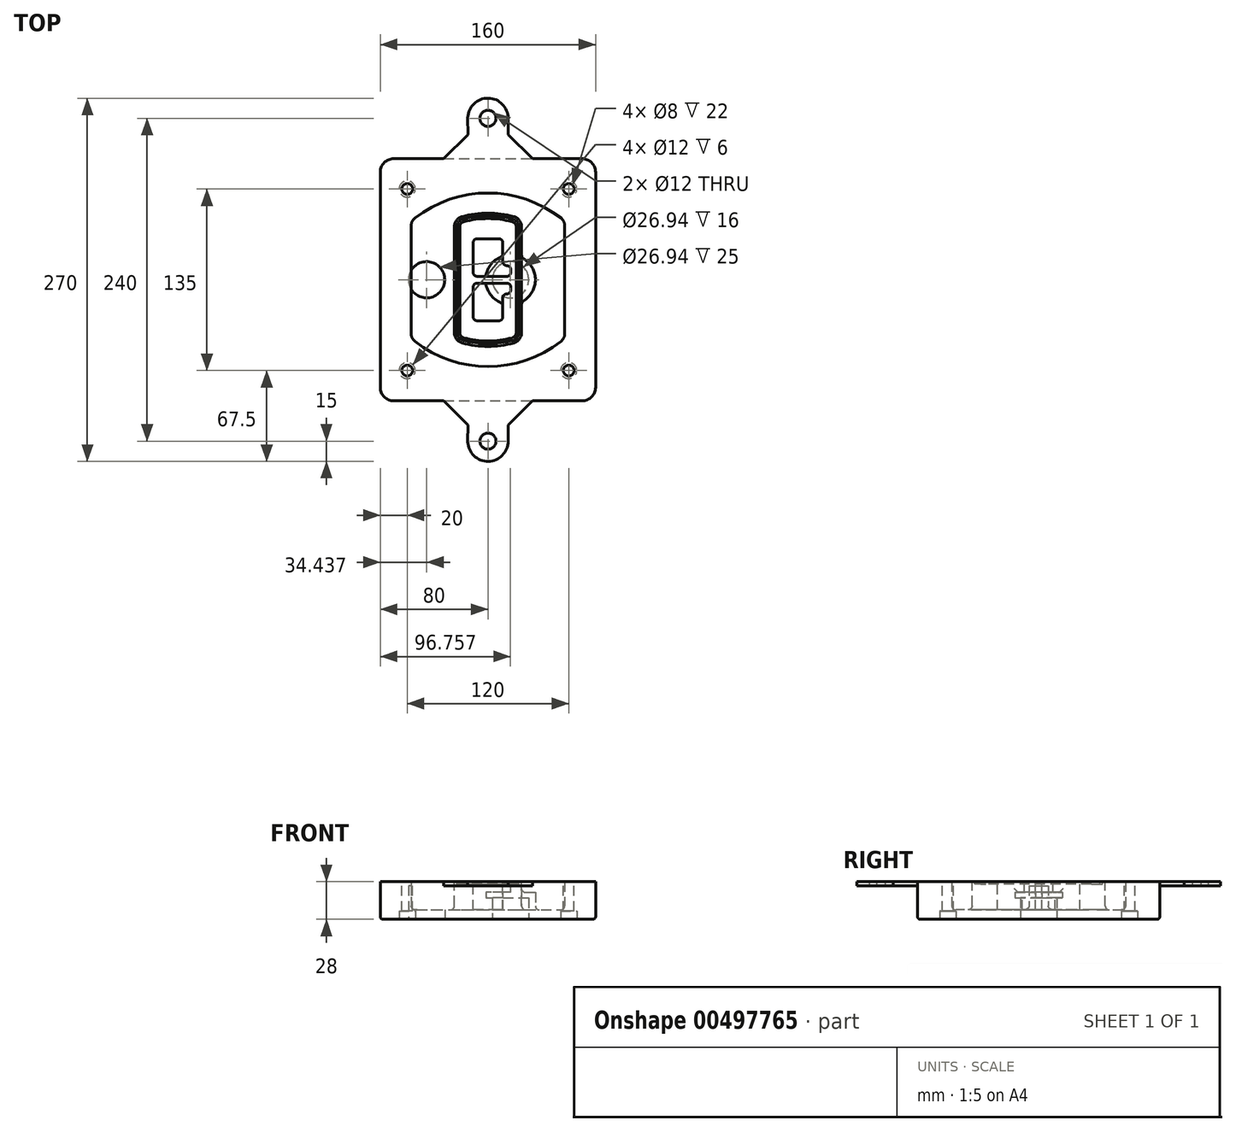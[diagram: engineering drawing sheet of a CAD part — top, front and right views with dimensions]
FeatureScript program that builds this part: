
annotation { "Feature Type Name" : "Feature", "Feature Type Description" : "" }
export const myFeature = defineFeature(function(context is Context, id is Id, definition is map)
    precondition{}
    {
        {
            var Q0;
            Q0=qCreatedBy(makeId("Top.planeOp"),FACE);
            var sketch = newSketch(context, id + "F0", { "sketchPlane" : qUnion([Q0])});
            skPoint(sketch, "E0.rect.middle", {"position": v(0, 0) * mm});
            skLineSegment(sketch, "E1.bottom", {"start": v(-70, -90) * mm, "end": v(70, -90) * mm});
            skLineSegment(sketch, "E1.top", {"start": v(-70, 90) * mm, "end": v(70, 90) * mm});
            skLineSegment(sketch, "E1.left", {"start": v(-80, -80) * mm, "end": v(-80, 80) * mm});
            skLineSegment(sketch, "E1.right", {"start": v(80, -80) * mm, "end": v(80, 80) * mm});
            skLineSegment(sketch, "E2", {"start": v(-80, 90) * mm, "end": v(80, -90) * mm, "construction": true});
            skLineSegment(sketch, "E3", {"start": v(80, 90) * mm, "end": v(-80, -90) * mm, "construction": true});
            skCircle(sketch, "E4", {"center": v(-60, 67.5) * mm, "radius": 4 * mm});
            skCircle(sketch, "E5", {"center": v(60, 67.5) * mm, "radius": 4 * mm});
            skCircle(sketch, "E6", {"center": v(60, -67.5) * mm, "radius": 4 * mm});
            skCircle(sketch, "E7", {"center": v(-60, -67.5) * mm, "radius": 4 * mm});
            skLineSegment(sketch, "E8", {"start": v(-60, 67.5) * mm, "end": v(60, 67.5) * mm, "construction": true});
            skLineSegment(sketch, "E9", {"start": v(60, 67.5) * mm, "end": v(60, -67.5) * mm, "construction": true});
            skLineSegment(sketch, "E10", {"start": v(60, -67.5) * mm, "end": v(-60, -67.5) * mm, "construction": true});
            skLineSegment(sketch, "E11", {"start": v(-60, -67.5) * mm, "end": v(-60, 67.5) * mm, "construction": true});
            skLineSegment(sketch, "E12", {"start": v(-60, 40.3) * mm, "end": v(-60, -40.3) * mm});
            skLineSegment(sketch, "E13", {"start": v(60, 40.3) * mm, "end": v(60, -40.3) * mm});
            skArc(sketch, "E14", {"start": v(56.15, 48.18) * mm, "mid": v(0, 67.5) * mm, "end": v(-56.15, 48.18) * mm});
            skArc(sketch, "E15", {"start": v(-56.15, -48.18) * mm, "mid": v(0, -67.5) * mm, "end": v(56.15, -48.18) * mm});
            skLineSegment(sketch, "E16", {"start": v(-60, 0) * mm, "end": v(60, 0) * mm, "construction": true});
            skPoint(sketch, "E17.visualSharp", {"position": v(-60, -45) * mm});
            skArc(sketch, "E17.filletArc", {"start": v(-60, -40.3) * mm, "mid": v(-58.99, -44.68) * mm, "end": v(-56.15, -48.18) * mm});
            skPoint(sketch, "E18.visualSharp", {"position": v(-60, 45) * mm});
            skArc(sketch, "E18.filletArc", {"start": v(-56.15, 48.18) * mm, "mid": v(-58.99, 44.68) * mm, "end": v(-60, 40.3) * mm});
            skPoint(sketch, "E19.visualSharp", {"position": v(60, 45) * mm});
            skArc(sketch, "E19.filletArc", {"start": v(60, 40.3) * mm, "mid": v(58.99, 44.68) * mm, "end": v(56.15, 48.18) * mm});
            skPoint(sketch, "E20.visualSharp", {"position": v(60, -45) * mm});
            skArc(sketch, "E20.filletArc", {"start": v(56.15, -48.18) * mm, "mid": v(58.99, -44.68) * mm, "end": v(60, -40.3) * mm});
            skPoint(sketch, "E21.visualSharp", {"position": v(-80, 90) * mm});
            skArc(sketch, "E21.filletArc", {"start": v(-70, 90) * mm, "mid": v(-77.07, 87.07) * mm, "end": v(-80, 80) * mm});
            skPoint(sketch, "E22.visualSharp", {"position": v(80, 90) * mm});
            skArc(sketch, "E22.filletArc", {"start": v(80, 80) * mm, "mid": v(77.07, 87.07) * mm, "end": v(70, 90) * mm});
            skPoint(sketch, "E23.visualSharp", {"position": v(80, -90) * mm});
            skArc(sketch, "E23.filletArc", {"start": v(70, -90) * mm, "mid": v(77.07, -87.07) * mm, "end": v(80, -80) * mm});
            skPoint(sketch, "E24.visualSharp", {"position": v(-80, -90) * mm});
            skArc(sketch, "E24.filletArc", {"start": v(-80, -80) * mm, "mid": v(-77.07, -87.07) * mm, "end": v(-70, -90) * mm});
            skArc(sketch, "E25.0", {"start": v(57, 40.3) * mm, "mid": v(56.3, 43.36) * mm, "end": v(54.3, 45.81) * mm});
            skLineSegment(sketch, "E25.1", {"start": v(57, 40.3) * mm, "end": v(57, -40.3) * mm});
            skArc(sketch, "E25.2", {"start": v(54.3, -45.81) * mm, "mid": v(56.3, -43.36) * mm, "end": v(57, -40.3) * mm});
            skArc(sketch, "E25.3", {"start": v(-54.3, -45.81) * mm, "mid": v(0, -64.5) * mm, "end": v(54.3, -45.81) * mm});
            skArc(sketch, "E25.4", {"start": v(-57, -40.3) * mm, "mid": v(-56.3, -43.36) * mm, "end": v(-54.3, -45.81) * mm});
            skArc(sketch, "E25.5", {"start": v(54.3, 45.81) * mm, "mid": v(0, 64.5) * mm, "end": v(-54.3, 45.81) * mm});
            skLineSegment(sketch, "E25.6", {"start": v(-57, 40.3) * mm, "end": v(-57, -40.3) * mm});
            skArc(sketch, "E25.7", {"start": v(-54.3, 45.81) * mm, "mid": v(-56.3, 43.36) * mm, "end": v(-57, 40.3) * mm});
            skArc(sketch, "E26.0", {"start": v(-58.62, 51.33) * mm, "mid": v(-62.58, 46.43) * mm, "end": v(-64, 40.3) * mm});
            skArc(sketch, "E26.1", {"start": v(58.62, 51.33) * mm, "mid": v(0, 71.5) * mm, "end": v(-58.62, 51.33) * mm});
            skArc(sketch, "E26.2", {"start": v(64, 40.3) * mm, "mid": v(62.58, 46.43) * mm, "end": v(58.62, 51.33) * mm});
            skLineSegment(sketch, "E26.3", {"start": v(64, 40.3) * mm, "end": v(64, -40.3) * mm});
            skArc(sketch, "E26.4", {"start": v(58.62, -51.33) * mm, "mid": v(62.58, -46.43) * mm, "end": v(64, -40.3) * mm});
            skLineSegment(sketch, "E26.5", {"start": v(-64, 40.3) * mm, "end": v(-64, -40.3) * mm});
            skArc(sketch, "E26.6", {"start": v(-58.62, -51.33) * mm, "mid": v(0, -71.5) * mm, "end": v(58.62, -51.33) * mm});
            skArc(sketch, "E26.7", {"start": v(-64, -40.3) * mm, "mid": v(-62.58, -46.43) * mm, "end": v(-58.62, -51.33) * mm});
            skSolve(sketch);
        }
        {
            var Q0;
            Q0=makeQuery(id+"F0.imprint","IMPRINT",FACE,{"disambiguationData":[TD([[makeQuery(id+"F0.imprint","IMPRINT",EDGE,{"derivedFrom":sQuery(id+"F0.wireOp",EDGE,"E1.bottom")}),1.0]])]});
            var Q1;
            Q1=makeQuery(id+"F0.imprint","IMPRINT",FACE,{"disambiguationData":[TD([[makeQuery(id+"F0.imprint","IMPRINT",EDGE,{"derivedFrom":sQuery(id+"F0.wireOp",EDGE,"E12")}),1.0]])]});
            var Q2;
            Q2=makeQuery(id+"F0.imprint","IMPRINT",FACE,{"disambiguationData":[TD([[makeQuery(id+"F0.imprint","IMPRINT",EDGE,{"derivedFrom":sQuery(id+"F0.wireOp",EDGE,"E25.0")}),1.0]])]});
            var Q3;
            Q3=makeQuery(id+"F0.imprint","IMPRINT",FACE,{"disambiguationData":[TD([[makeQuery(id+"F0.imprint","IMPRINT",EDGE,{"derivedFrom":sQuery(id+"F0.wireOp",EDGE,"E12")}),-1.0]])]});
            extrude(context, id + "F1", {"entities" : qUnion([Q0, Q1, Q2, Q3]), "oppositeDirection" : true, "depth" : 25 * mm});
        }
        {
            var Q0;
            Q0=makeQuery(id+"F0.imprint","IMPRINT",FACE,{"disambiguationData":[TD([[makeQuery(id+"F0.imprint","IMPRINT",EDGE,{"derivedFrom":sQuery(id+"F0.wireOp",EDGE,"E12")}),1.0]])]});
            extrude(context, id + "F2", {"entities" : qUnion([Q0]), "operationType" : NewBodyOperationType.ADD, "depth" : 3 * mm});
        }
        {
            var Q0;
            Q0=makeQuery(id+"F0.imprint","IMPRINT",FACE,{"disambiguationData":[TD([[makeQuery(id+"F0.imprint","IMPRINT",EDGE,{"derivedFrom":sQuery(id+"F0.wireOp",EDGE,"E25.0")}),1.0]])]});
            extrude(context, id + "F3", {"entities" : qUnion([Q0]), "operationType" : NewBodyOperationType.REMOVE, "oppositeDirection" : true, "depth" : 18 * mm});
        }
        {
            var Q0;
            Q0=makeQuery(id+"F2.opExtrude","CAP_FACE",FACE,{"disambiguationData":[OSD([sQuery(id+"F0.wireOp",EDGE,"E12"),sQuery(id+"F0.wireOp",EDGE,"E13"),sQuery(id+"F0.wireOp",EDGE,"E14"),sQuery(id+"F0.wireOp",EDGE,"E15"),sQuery(id+"F0.wireOp",EDGE,"E17.filletArc"),sQuery(id+"F0.wireOp",EDGE,"E18.filletArc"),sQuery(id+"F0.wireOp",EDGE,"E19.filletArc"),sQuery(id+"F0.wireOp",EDGE,"E20.filletArc"),sQuery(id+"F0.wireOp",EDGE,"E25.0"),sQuery(id+"F0.wireOp",EDGE,"E25.1"),sQuery(id+"F0.wireOp",EDGE,"E25.2"),sQuery(id+"F0.wireOp",EDGE,"E25.3"),sQuery(id+"F0.wireOp",EDGE,"E25.4"),sQuery(id+"F0.wireOp",EDGE,"E25.5"),sQuery(id+"F0.wireOp",EDGE,"E25.6"),sQuery(id+"F0.wireOp",EDGE,"E25.7")])],"isStart":false});
            var sketch = newSketch(context, id + "F4", { "sketchPlane" : qUnion([Q0])});
            skArc(sketch, "E27.0", {"start": v(-19.08, -46.97) * mm, "mid": v(0, -49.5) * mm, "end": v(19.08, -46.97) * mm});
            skArc(sketch, "E28.0", {"start": v(19.08, 46.97) * mm, "mid": v(0, 49.5) * mm, "end": v(-19.08, 46.97) * mm});
            skLineSegment(sketch, "E29", {"start": v(-25, 39.25) * mm, "end": v(-25, -39.25) * mm});
            skLineSegment(sketch, "E30", {"start": v(25, 39.25) * mm, "end": v(25, -39.25) * mm});
            skLineSegment(sketch, "E31", {"start": v(-25, 45.1) * mm, "end": v(25, 45.1) * mm, "construction": true});
            skLineSegment(sketch, "E32", {"start": v(-25, -45.1) * mm, "end": v(25, -45.1) * mm, "construction": true});
            skPoint(sketch, "E33.visualSharp", {"position": v(-25, 45.1) * mm});
            skArc(sketch, "E33.filletArc", {"start": v(-19.08, 46.97) * mm, "mid": v(-23.35, 44.11) * mm, "end": v(-25, 39.25) * mm});
            skPoint(sketch, "E34.visualSharp", {"position": v(25, 45.1) * mm});
            skArc(sketch, "E34.filletArc", {"start": v(25, 39.25) * mm, "mid": v(23.35, 44.11) * mm, "end": v(19.08, 46.97) * mm});
            skPoint(sketch, "E35.visualSharp", {"position": v(25, -45.1) * mm});
            skArc(sketch, "E35.filletArc", {"start": v(19.08, -46.97) * mm, "mid": v(23.35, -44.11) * mm, "end": v(25, -39.25) * mm});
            skPoint(sketch, "E36.visualSharp", {"position": v(-25, -45.1) * mm});
            skArc(sketch, "E36.filletArc", {"start": v(-25, -39.25) * mm, "mid": v(-23.35, -44.11) * mm, "end": v(-19.08, -46.97) * mm});
            skArc(sketch, "E37.0", {"start": v(54.3, 45.81) * mm, "mid": v(0, 64.5) * mm, "end": v(-54.3, 45.81) * mm});
            skArc(sketch, "E37.1", {"start": v(-54.3, 45.81) * mm, "mid": v(-56.3, 43.36) * mm, "end": v(-57, 40.3) * mm});
            skLineSegment(sketch, "E37.2", {"start": v(-57, 40.3) * mm, "end": v(-57, -40.3) * mm});
            skArc(sketch, "E37.3", {"start": v(-57, -40.3) * mm, "mid": v(-56.3, -43.36) * mm, "end": v(-54.3, -45.81) * mm});
            skArc(sketch, "E37.4", {"start": v(-54.3, -45.81) * mm, "mid": v(0, -64.5) * mm, "end": v(54.3, -45.81) * mm});
            skArc(sketch, "E37.5", {"start": v(54.3, -45.81) * mm, "mid": v(56.3, -43.36) * mm, "end": v(57, -40.3) * mm});
            skLineSegment(sketch, "E37.6", {"start": v(57, 40.3) * mm, "end": v(57, -40.3) * mm});
            skArc(sketch, "E37.7", {"start": v(57, 40.3) * mm, "mid": v(56.3, 43.36) * mm, "end": v(54.3, 45.81) * mm});
            skLineSegment(sketch, "E38.0", {"start": v(23, 39.25) * mm, "end": v(23, -39.25) * mm});
            skArc(sketch, "E38.1", {"start": v(18.56, -45.04) * mm, "mid": v(21.76, -42.9) * mm, "end": v(23, -39.25) * mm});
            skArc(sketch, "E38.2", {"start": v(-18.56, -45.04) * mm, "mid": v(0, -47.5) * mm, "end": v(18.56, -45.04) * mm});
            skArc(sketch, "E38.3", {"start": v(-23, -39.25) * mm, "mid": v(-21.76, -42.9) * mm, "end": v(-18.56, -45.04) * mm});
            skLineSegment(sketch, "E38.4", {"start": v(-23, 39.25) * mm, "end": v(-23, -39.25) * mm});
            skArc(sketch, "E38.5", {"start": v(23, 39.25) * mm, "mid": v(21.76, 42.9) * mm, "end": v(18.56, 45.04) * mm});
            skArc(sketch, "E38.6", {"start": v(-18.56, 45.04) * mm, "mid": v(-21.76, 42.9) * mm, "end": v(-23, 39.25) * mm});
            skArc(sketch, "E38.7", {"start": v(18.56, 45.04) * mm, "mid": v(0, 47.5) * mm, "end": v(-18.56, 45.04) * mm});
            skArc(sketch, "E39.0", {"start": v(21, 39.25) * mm, "mid": v(20.18, 41.68) * mm, "end": v(18.04, 43.1) * mm});
            skLineSegment(sketch, "E39.1", {"start": v(21, 39.25) * mm, "end": v(21, -39.25) * mm});
            skArc(sketch, "E39.2", {"start": v(18.04, -43.1) * mm, "mid": v(20.18, -41.68) * mm, "end": v(21, -39.25) * mm});
            skArc(sketch, "E39.3", {"start": v(-18.04, -43.1) * mm, "mid": v(0, -45.5) * mm, "end": v(18.04, -43.1) * mm});
            skArc(sketch, "E39.4", {"start": v(-21, -39.25) * mm, "mid": v(-20.18, -41.68) * mm, "end": v(-18.04, -43.1) * mm});
            skArc(sketch, "E39.5", {"start": v(18.04, 43.1) * mm, "mid": v(0, 45.5) * mm, "end": v(-18.04, 43.1) * mm});
            skLineSegment(sketch, "E39.6", {"start": v(-21, 39.25) * mm, "end": v(-21, -39.25) * mm});
            skArc(sketch, "E39.7", {"start": v(-18.04, 43.1) * mm, "mid": v(-20.18, 41.68) * mm, "end": v(-21, 39.25) * mm});
            skLineSegment(sketch, "E40", {"start": v(-25, 0) * mm, "end": v(25, 0) * mm, "construction": true});
            skLineSegment(sketch, "E41", {"start": v(-11, 5.5) * mm, "end": v(-11, 27.5) * mm});
            skLineSegment(sketch, "E42", {"start": v(-8, 30.5) * mm, "end": v(8, 30.5) * mm});
            skLineSegment(sketch, "E43", {"start": v(11, 27.5) * mm, "end": v(11, 13.5) * mm});
            skLineSegment(sketch, "E44", {"start": v(14, 10.5) * mm, "end": v(14, 10.5) * mm});
            skLineSegment(sketch, "E45", {"start": v(17, 7.5) * mm, "end": v(17, 5.5) * mm});
            skLineSegment(sketch, "E46", {"start": v(14, 2.5) * mm, "end": v(-8, 2.5) * mm});
            skPoint(sketch, "E47.visualSharp", {"position": v(-11, 30.5) * mm});
            skArc(sketch, "E47.filletArc", {"start": v(-8, 30.5) * mm, "mid": v(-10.12, 29.62) * mm, "end": v(-11, 27.5) * mm});
            skPoint(sketch, "E48.visualSharp", {"position": v(11, 30.5) * mm});
            skArc(sketch, "E48.filletArc", {"start": v(11, 27.5) * mm, "mid": v(10.12, 29.62) * mm, "end": v(8, 30.5) * mm});
            skPoint(sketch, "E49.visualSharp", {"position": v(11, 10.5) * mm});
            skArc(sketch, "E49.filletArc", {"start": v(11, 13.5) * mm, "mid": v(11.88, 11.38) * mm, "end": v(14, 10.5) * mm});
            skPoint(sketch, "E50.visualSharp", {"position": v(17, 10.5) * mm});
            skArc(sketch, "E50.filletArc", {"start": v(17, 7.5) * mm, "mid": v(16.12, 9.62) * mm, "end": v(14, 10.5) * mm});
            skPoint(sketch, "E51.visualSharp", {"position": v(17, 2.5) * mm});
            skArc(sketch, "E51.filletArc", {"start": v(14, 2.5) * mm, "mid": v(16.12, 3.38) * mm, "end": v(17, 5.5) * mm});
            skPoint(sketch, "E52.visualSharp", {"position": v(-11, 2.5) * mm});
            skArc(sketch, "E52.filletArc", {"start": v(-11, 5.5) * mm, "mid": v(-10.12, 3.38) * mm, "end": v(-8, 2.5) * mm});
            skLineSegment(sketch, "E53.0.MirrorCS", {"start": v(14, -2.5) * mm, "end": v(-8, -2.5) * mm});
            skArc(sketch, "E54.0.MirrorCS", {"start": v(-11, -5.5) * mm, "mid": v(-10.12, -3.38) * mm, "end": v(-8, -2.5) * mm});
            skLineSegment(sketch, "E55.0.MirrorCS", {"start": v(-11, -5.5) * mm, "end": v(-11, -27.5) * mm});
            skArc(sketch, "E56.0.MirrorCS", {"start": v(-8, -30.5) * mm, "mid": v(-10.12, -29.62) * mm, "end": v(-11, -27.5) * mm});
            skLineSegment(sketch, "E57.0.MirrorCS", {"start": v(-8, -30.5) * mm, "end": v(8, -30.5) * mm});
            skArc(sketch, "E58.0.MirrorCS", {"start": v(11, -27.5) * mm, "mid": v(10.12, -29.62) * mm, "end": v(8, -30.5) * mm});
            skLineSegment(sketch, "E59.0.MirrorCS", {"start": v(11, -27.5) * mm, "end": v(11, -13.5) * mm});
            skArc(sketch, "E60.0.MirrorCS", {"start": v(11, -13.5) * mm, "mid": v(11.88, -11.38) * mm, "end": v(14, -10.5) * mm});
            skArc(sketch, "E61.0.MirrorCS", {"start": v(17, -7.5) * mm, "mid": v(16.12, -9.62) * mm, "end": v(14, -10.5) * mm});
            skLineSegment(sketch, "E62.0.MirrorCS", {"start": v(17, -7.5) * mm, "end": v(17, -5.5) * mm});
            skArc(sketch, "E63.0.MirrorCS", {"start": v(14, -2.5) * mm, "mid": v(16.12, -3.38) * mm, "end": v(17, -5.5) * mm});
            skSolve(sketch);
        }
        {
            var Q0;
            Q0=makeQuery(id+"F4.imprint","IMPRINT",FACE,{"disambiguationData":[TD([[makeQuery(id+"F4.imprint","IMPRINT",EDGE,{"derivedFrom":sQuery(id+"F4.wireOp",EDGE,"E27.0")}),1.0]])]});
            var Q1;
            Q1=makeQuery(id+"F4.imprint","IMPRINT",FACE,{"disambiguationData":[TD([[makeQuery(id+"F4.imprint","IMPRINT",EDGE,{"derivedFrom":sQuery(id+"F4.wireOp",EDGE,"E38.0")}),-1.0]])]});
            var Q2;
            Q2=makeQuery(id+"F4.imprint","IMPRINT",FACE,{"disambiguationData":[TD([[makeQuery(id+"F4.imprint","IMPRINT",EDGE,{"derivedFrom":sQuery(id+"F4.wireOp",EDGE,"E39.0")}),1.0]])]});
            extrude(context, id + "F5", {"entities" : qUnion([Q0, Q1, Q2]), "operationType" : NewBodyOperationType.ADD, "endBound" : BoundingType.UP_TO_NEXT, "oppositeDirection" : true, "depth" : 25 * mm});
        }
        {
            var Q0;
            Q0=makeQuery(id+"F4.imprint","IMPRINT",FACE,{"disambiguationData":[TD([[makeQuery(id+"F4.imprint","IMPRINT",EDGE,{"derivedFrom":sQuery(id+"F4.wireOp",EDGE,"E38.0")}),-1.0]])]});
            extrude(context, id + "F6", {"entities" : qUnion([Q0]), "operationType" : NewBodyOperationType.REMOVE, "oppositeDirection" : true, "depth" : 2 * mm});
        }
        {
            var Q0;
            Q0=makeQuery(id+"F1.opExtrude","CAP_FACE",FACE,{"disambiguationData":[OSD([sQuery(id+"F0.wireOp",EDGE,"E1.bottom"),sQuery(id+"F0.wireOp",EDGE,"E1.top"),sQuery(id+"F0.wireOp",EDGE,"E1.left"),sQuery(id+"F0.wireOp",EDGE,"E1.right"),sQuery(id+"F0.wireOp",EDGE,"E4"),sQuery(id+"F0.wireOp",EDGE,"E5"),sQuery(id+"F0.wireOp",EDGE,"E6"),sQuery(id+"F0.wireOp",EDGE,"E7"),sQuery(id+"F0.wireOp",EDGE,"E21.filletArc"),sQuery(id+"F0.wireOp",EDGE,"E22.filletArc"),sQuery(id+"F0.wireOp",EDGE,"E23.filletArc"),sQuery(id+"F0.wireOp",EDGE,"E24.filletArc")])],"isStart":false});
            var sketch = newSketch(context, id + "F7", { "sketchPlane" : qUnion([Q0])});
            skCircle(sketch, "E64", {"center": v(16.76, 0) * mm, "radius": 13.47 * mm});
            skCircle(sketch, "E65", {"center": v(-45.56, 0) * mm, "radius": 13.47 * mm});
            skLineSegment(sketch, "E66", {"start": v(80, 0) * mm, "end": v(-80, 0) * mm});
            skCircle(sketch, "E67", {"center": v(16.76, 0) * mm, "radius": 18.47 * mm});
            skCircle(sketch, "E68", {"center": v(60, -67.5) * mm, "radius": 6 * mm});
            skCircle(sketch, "E69", {"center": v(-60, -67.5) * mm, "radius": 6 * mm});
            skCircle(sketch, "E70", {"center": v(-60, 67.5) * mm, "radius": 6 * mm});
            skCircle(sketch, "E71", {"center": v(60, 67.5) * mm, "radius": 6 * mm});
            skSolve(sketch);
        }
        {
            var Q0;
            {var subQ1=sQuery(id+"F7.wireOp",EDGE,"E66");var subQ4=sQuery(id+"F7.wireOp",EDGE,"E64");var subQ6=makeQuery(id+"F7.imprint","INTERSECT",VERTEX,{"disambiguationData":[OD(0.0)],"derivedFrom":[subQ4,subQ1]});Q0=makeQuery(id+"F7.imprint","IMPRINT",FACE,{"disambiguationData":[TD([[makeQuery(id+"F7.imprint","IMPRINT",EDGE,{"disambiguationData":[TD([[subQ6,-1.0]])],"derivedFrom":subQ4}),-1.0]])]});}
            var Q1;
            {var subQ0=sQuery(id+"F7.wireOp",EDGE,"E66");var subQ1=sQuery(id+"F7.wireOp",EDGE,"E64");var subQ3=makeQuery(id+"F7.imprint","INTERSECT",VERTEX,{"disambiguationData":[OD(0.0)],"derivedFrom":[subQ1,subQ0]});Q1=makeQuery(id+"F7.imprint","IMPRINT",FACE,{"disambiguationData":[TD([[makeQuery(id+"F7.imprint","IMPRINT",EDGE,{"disambiguationData":[TD([[subQ3,-1.0]])],"derivedFrom":subQ1}),1.0]])]});}
            var Q2;
            {var subQ0=sQuery(id+"F7.wireOp",EDGE,"E66");var subQ1=sQuery(id+"F7.wireOp",EDGE,"E64");var subQ3=makeQuery(id+"F7.imprint","INTERSECT",VERTEX,{"disambiguationData":[OD(0.0)],"derivedFrom":[subQ1,subQ0]});Q2=makeQuery(id+"F7.imprint","IMPRINT",FACE,{"disambiguationData":[TD([[makeQuery(id+"F7.imprint","IMPRINT",EDGE,{"disambiguationData":[TD([[subQ3,1.0]])],"derivedFrom":subQ1}),1.0]])]});}
            var Q3;
            {var subQ1=sQuery(id+"F7.wireOp",EDGE,"E66");var subQ4=sQuery(id+"F7.wireOp",EDGE,"E64");var subQ6=makeQuery(id+"F7.imprint","INTERSECT",VERTEX,{"disambiguationData":[OD(0.0)],"derivedFrom":[subQ4,subQ1]});Q3=makeQuery(id+"F7.imprint","IMPRINT",FACE,{"disambiguationData":[TD([[makeQuery(id+"F7.imprint","IMPRINT",EDGE,{"disambiguationData":[TD([[subQ6,1.0]])],"derivedFrom":subQ4}),-1.0]])]});}
            extrude(context, id + "F8", {"entities" : qUnion([Q0, Q1, Q2, Q3]), "operationType" : NewBodyOperationType.ADD, "oppositeDirection" : true, "depth" : 20 * mm});
        }
        {
            var Q0;
            {var subQ0=sQuery(id+"F7.wireOp",EDGE,"E66");var subQ1=sQuery(id+"F7.wireOp",EDGE,"E64");var subQ3=makeQuery(id+"F7.imprint","INTERSECT",VERTEX,{"disambiguationData":[OD(0.0)],"derivedFrom":[subQ1,subQ0]});Q0=makeQuery(id+"F7.imprint","IMPRINT",FACE,{"disambiguationData":[TD([[makeQuery(id+"F7.imprint","IMPRINT",EDGE,{"disambiguationData":[TD([[subQ3,-1.0]])],"derivedFrom":subQ1}),1.0]])]});}
            var Q1;
            {var subQ0=sQuery(id+"F7.wireOp",EDGE,"E66");var subQ1=sQuery(id+"F7.wireOp",EDGE,"E64");var subQ3=makeQuery(id+"F7.imprint","INTERSECT",VERTEX,{"disambiguationData":[OD(0.0)],"derivedFrom":[subQ1,subQ0]});Q1=makeQuery(id+"F7.imprint","IMPRINT",FACE,{"disambiguationData":[TD([[makeQuery(id+"F7.imprint","IMPRINT",EDGE,{"disambiguationData":[TD([[subQ3,1.0]])],"derivedFrom":subQ1}),1.0]])]});}
            extrude(context, id + "F9", {"entities" : qUnion([Q0, Q1]), "operationType" : NewBodyOperationType.REMOVE, "oppositeDirection" : true, "depth" : 16 * mm});
        }
        {
            var Q0;
            {var subQ0=sQuery(id+"F7.wireOp",EDGE,"E66");var subQ1=sQuery(id+"F7.wireOp",EDGE,"E65");var subQ3=makeQuery(id+"F7.imprint","INTERSECT",VERTEX,{"disambiguationData":[OD(0.0)],"derivedFrom":[subQ1,subQ0]});Q0=makeQuery(id+"F7.imprint","IMPRINT",FACE,{"disambiguationData":[TD([[makeQuery(id+"F7.imprint","IMPRINT",EDGE,{"disambiguationData":[TD([[subQ3,-1.0]])],"derivedFrom":subQ1}),1.0]])]});}
            var Q1;
            {var subQ0=sQuery(id+"F7.wireOp",EDGE,"E66");var subQ1=sQuery(id+"F7.wireOp",EDGE,"E65");var subQ3=makeQuery(id+"F7.imprint","INTERSECT",VERTEX,{"disambiguationData":[OD(0.0)],"derivedFrom":[subQ1,subQ0]});Q1=makeQuery(id+"F7.imprint","IMPRINT",FACE,{"disambiguationData":[TD([[makeQuery(id+"F7.imprint","IMPRINT",EDGE,{"disambiguationData":[TD([[subQ3,1.0]])],"derivedFrom":subQ1}),1.0]])]});}
            extrude(context, id + "F10", {"entities" : qUnion([Q0, Q1]), "operationType" : NewBodyOperationType.REMOVE, "oppositeDirection" : true, "depth" : 25 * mm});
        }
        {
            var Q0;
            Q0=makeQuery(id+"F7.imprint","IMPRINT",FACE,{"disambiguationData":[TD([[makeQuery(id+"F7.imprint","IMPRINT",EDGE,{"derivedFrom":sQuery(id+"F7.wireOp",EDGE,"E68")}),1.0]])]});
            var Q1;
            Q1=makeQuery(id+"F7.imprint","IMPRINT",FACE,{"disambiguationData":[TD([[makeQuery(id+"F7.imprint","IMPRINT",EDGE,{"derivedFrom":makeQuery(id+"F1.opExtrude","CAP_EDGE",EDGE,{"disambiguationData":[OSD([sQuery(id+"F0.wireOp",EDGE,"E5")])],"isStart":false})}),-1.0]])]});
            var Q2;
            Q2=makeQuery(id+"F7.imprint","IMPRINT",FACE,{"disambiguationData":[TD([[makeQuery(id+"F7.imprint","IMPRINT",EDGE,{"derivedFrom":sQuery(id+"F7.wireOp",EDGE,"E69")}),1.0]])]});
            var Q3;
            Q3=makeQuery(id+"F7.imprint","IMPRINT",FACE,{"disambiguationData":[TD([[makeQuery(id+"F7.imprint","IMPRINT",EDGE,{"derivedFrom":makeQuery(id+"F1.opExtrude","CAP_EDGE",EDGE,{"disambiguationData":[OSD([sQuery(id+"F0.wireOp",EDGE,"E4")])],"isStart":false})}),-1.0]])]});
            var Q4;
            Q4=makeQuery(id+"F7.imprint","IMPRINT",FACE,{"disambiguationData":[TD([[makeQuery(id+"F7.imprint","IMPRINT",EDGE,{"derivedFrom":sQuery(id+"F7.wireOp",EDGE,"E70")}),1.0]])]});
            var Q5;
            Q5=makeQuery(id+"F7.imprint","IMPRINT",FACE,{"disambiguationData":[TD([[makeQuery(id+"F7.imprint","IMPRINT",EDGE,{"derivedFrom":makeQuery(id+"F1.opExtrude","CAP_EDGE",EDGE,{"disambiguationData":[OSD([sQuery(id+"F0.wireOp",EDGE,"E7")])],"isStart":false})}),-1.0]])]});
            var Q6;
            Q6=makeQuery(id+"F7.imprint","IMPRINT",FACE,{"disambiguationData":[TD([[makeQuery(id+"F7.imprint","IMPRINT",EDGE,{"derivedFrom":sQuery(id+"F7.wireOp",EDGE,"E71")}),1.0]])]});
            var Q7;
            Q7=makeQuery(id+"F7.imprint","IMPRINT",FACE,{"disambiguationData":[TD([[makeQuery(id+"F7.imprint","IMPRINT",EDGE,{"derivedFrom":makeQuery(id+"F1.opExtrude","CAP_EDGE",EDGE,{"disambiguationData":[OSD([sQuery(id+"F0.wireOp",EDGE,"E6")])],"isStart":false})}),-1.0]])]});
            extrude(context, id + "F11", {"entities" : qUnion([Q0, Q1, Q2, Q3, Q4, Q5, Q6, Q7]), "operationType" : NewBodyOperationType.REMOVE, "oppositeDirection" : true, "depth" : 6 * mm});
        }
        {
            var Q0;
            Q0=makeQuery(id+"F9.boolean.opBoolean","COPY",FACE,{"derivedFrom":makeQuery(id+"F9.opExtrude","CAP_FACE",FACE,{"disambiguationData":[OSD([sQuery(id+"F7.wireOp",EDGE,"E64")])],"isStart":false})});
            var sketch = newSketch(context, id + "F12", { "sketchPlane" : qUnion([Q0])});
            skArc(sketch, "E72.0", {"start": v(11, 17.55) * mm, "mid": v(2.57, 11.82) * mm, "end": v(-1.54, 2.5) * mm});
            skArc(sketch, "E72.1", {"start": v(-1.54, -2.5) * mm, "mid": v(2.57, -11.82) * mm, "end": v(11, -17.55) * mm});
            skLineSegment(sketch, "E73", {"start": v(-1.54, -2.5) * mm, "end": v(14, -2.5) * mm});
            skLineSegment(sketch, "E74.0", {"start": v(14, 2.5) * mm, "end": v(-1.54, 2.5) * mm});
            skArc(sketch, "E74.1", {"start": v(14, 2.5) * mm, "mid": v(16.12, 3.38) * mm, "end": v(17, 5.5) * mm});
            skLineSegment(sketch, "E74.2", {"start": v(17, 7.5) * mm, "end": v(17, 5.5) * mm});
            skArc(sketch, "E74.3", {"start": v(17, 7.5) * mm, "mid": v(16.12, 9.62) * mm, "end": v(14, 10.5) * mm});
            skArc(sketch, "E74.4", {"start": v(11, 13.5) * mm, "mid": v(11.88, 11.38) * mm, "end": v(14, 10.5) * mm});
            skLineSegment(sketch, "E74.5", {"start": v(11, 17.55) * mm, "end": v(11, 13.5) * mm});
            skLineSegment(sketch, "E74.7", {"start": v(14, -2.5) * mm, "end": v(-1.54, -2.5) * mm});
            skArc(sketch, "E74.8", {"start": v(14, -2.5) * mm, "mid": v(16.12, -3.38) * mm, "end": v(17, -5.5) * mm});
            skLineSegment(sketch, "E74.9", {"start": v(17, -7.5) * mm, "end": v(17, -5.5) * mm});
            skArc(sketch, "E74.10", {"start": v(17, -7.5) * mm, "mid": v(16.12, -9.62) * mm, "end": v(14, -10.5) * mm});
            skArc(sketch, "E74.11", {"start": v(11, -13.5) * mm, "mid": v(11.88, -11.38) * mm, "end": v(14, -10.5) * mm});
            skLineSegment(sketch, "E74.12", {"start": v(11, -17.55) * mm, "end": v(11, -13.5) * mm});
            skPoint(sketch, "E75.orphan", {"position": v(11, -27.5) * mm});
            skPoint(sketch, "E76.orphan", {"position": v(-8, -2.5) * mm});
            skPoint(sketch, "E77.orphan", {"position": v(-8, 2.5) * mm});
            skPoint(sketch, "E78.orphan", {"position": v(11, 27.5) * mm});
            skSolve(sketch);
        }
        {
            var Q0;
            {var subQ7=sQuery(id+"F12.wireOp",EDGE,"E72.0");var subQ14=sQuery(id+"F12.wireOp",EDGE,"E72.1");var subQ16=sQuery(id+"F12.wireOp",EDGE,"E74.1");var subQ18=sQuery(id+"F12.wireOp",EDGE,"E74.8");Q0=qUnion([makeQuery(id+"F12.imprint","IMPRINT",FACE,{"disambiguationData":[TD([[makeQuery(id+"F12.imprint","IMPRINT",EDGE,{"derivedFrom":subQ7}),1.0]])]}),makeQuery(id+"F12.imprint","IMPRINT",FACE,{"disambiguationData":[TD([[makeQuery(id+"F12.imprint","IMPRINT",EDGE,{"derivedFrom":subQ14}),1.0]])]}),makeQuery(id+"F12.imprint","IMPRINT",FACE,{"disambiguationData":[TD([[makeQuery(id+"F12.imprint","IMPRINT",EDGE,{"derivedFrom":subQ16}),1.0]])]}),makeQuery(id+"F12.imprint","IMPRINT",FACE,{"disambiguationData":[TD([[makeQuery(id+"F12.imprint","IMPRINT",EDGE,{"derivedFrom":subQ18}),-1.0]])]})]);}
            var Q1;
            Q1=makeQuery(id+"F5.boolean.opBoolean","SPLIT",FACE,{"disambiguationData":[TD([makeQuery(id+"F5.opExtrude","SWEPT_FACE",FACE,{"disambiguationData":[OSD([sQuery(id+"F4.wireOp",EDGE,"E41")])]})])],"derivedFrom":makeQuery(id+"F3.boolean.opBoolean","COPY",FACE,{"derivedFrom":makeQuery(id+"F3.opExtrude","CAP_FACE",FACE,{"disambiguationData":[OSD([sQuery(id+"F0.wireOp",EDGE,"E25.0"),sQuery(id+"F0.wireOp",EDGE,"E25.1"),sQuery(id+"F0.wireOp",EDGE,"E25.2"),sQuery(id+"F0.wireOp",EDGE,"E25.3"),sQuery(id+"F0.wireOp",EDGE,"E25.4"),sQuery(id+"F0.wireOp",EDGE,"E25.5"),sQuery(id+"F0.wireOp",EDGE,"E25.6"),sQuery(id+"F0.wireOp",EDGE,"E25.7")])],"isStart":false})})});
            extrude(context, id + "F13", {"entities" : qUnion([Q0]), "operationType" : NewBodyOperationType.REMOVE, "endBound" : BoundingType.UP_TO_SURFACE, "endBoundEntityFace" : qUnion([Q1]), "depth" : 25 * mm});
        }
        {
            var Q0;
            Q0=makeQuery(id+"F3.boolean.opBoolean","COPY",EDGE,{"derivedFrom":makeQuery(id+"F3.opExtrude","CAP_EDGE",EDGE,{"disambiguationData":[OSD([sQuery(id+"F0.wireOp",EDGE,"E25.6")])],"isStart":false})});
            var Q1;
            Q1=makeQuery(id+"F8.boolean.opBoolean","INTERSECT",EDGE,{"derivedFrom":[makeQuery(id+"F5.opExtrude","SWEPT_FACE",FACE,{"disambiguationData":[OSD([sQuery(id+"F4.wireOp",EDGE,"E30")])]}),makeQuery(id+"F8.opExtrude","CAP_FACE",FACE,{"disambiguationData":[OSD([sQuery(id+"F7.wireOp",EDGE,"E67")])],"isStart":false})]});
            var Q2;
            Q2=makeQuery(id+"F8.boolean.opBoolean","INTERSECT",EDGE,{"disambiguationData":[OD(1.0)],"derivedFrom":[makeQuery(id+"F5.opExtrude","SWEPT_FACE",FACE,{"disambiguationData":[OSD([sQuery(id+"F4.wireOp",EDGE,"E30")])]}),makeQuery(id+"F8.opExtrude","SWEPT_FACE",FACE,{"disambiguationData":[OSD([sQuery(id+"F7.wireOp",EDGE,"E67")])]})]});
            var Q3;
            {var subQ0=sQuery(id+"F4.wireOp",EDGE,"E30");Q3=makeQuery(id+"F8.boolean.opBoolean","SPLIT",EDGE,{"disambiguationData":[TD([makeQuery(id+"F5.opExtrude","SWEPT_FACE",FACE,{"disambiguationData":[OSD([sQuery(id+"F4.wireOp",EDGE,"E35.filletArc")])]})])],"derivedFrom":makeQuery(id+"F5.opExtrude","CAP_EDGE",EDGE,{"disambiguationData":[OSD([subQ0])],"isStart":false})});}
            var Q4;
            {var subQ0=sQuery(id+"F0.wireOp",EDGE,"E25.7");var subQ1=sQuery(id+"F0.wireOp",EDGE,"E25.1");var subQ2=sQuery(id+"F0.wireOp",EDGE,"E25.6");var subQ3=sQuery(id+"F0.wireOp",EDGE,"E25.5");var subQ4=sQuery(id+"F0.wireOp",EDGE,"E25.4");var subQ5=sQuery(id+"F0.wireOp",EDGE,"E25.0");var subQ6=sQuery(id+"F0.wireOp",EDGE,"E25.2");var subQ7=sQuery(id+"F0.wireOp",EDGE,"E25.3");Q4=makeQuery(id+"F8.boolean.opBoolean","INTERSECT",EDGE,{"derivedFrom":[makeQuery(id+"F5.boolean.opBoolean","SPLIT",FACE,{"disambiguationData":[TD([makeQuery(id+"F2.opExtrude","SWEPT_FACE",FACE,{"disambiguationData":[OSD([subQ5])]})])],"derivedFrom":makeQuery(id+"F3.boolean.opBoolean","COPY",FACE,{"derivedFrom":makeQuery(id+"F3.opExtrude","CAP_FACE",FACE,{"disambiguationData":[OSD([subQ5,subQ1,subQ6,subQ7,subQ4,subQ3,subQ2,subQ0])],"isStart":false})})}),makeQuery(id+"F8.opExtrude","SWEPT_FACE",FACE,{"disambiguationData":[OSD([sQuery(id+"F7.wireOp",EDGE,"E67")])]})]});}
            var Q5;
            Q5=makeQuery(id+"F8.boolean.opBoolean","INTERSECT",EDGE,{"disambiguationData":[OD(0.0)],"derivedFrom":[makeQuery(id+"F5.opExtrude","SWEPT_FACE",FACE,{"disambiguationData":[OSD([sQuery(id+"F4.wireOp",EDGE,"E30")])]}),makeQuery(id+"F8.opExtrude","SWEPT_FACE",FACE,{"disambiguationData":[OSD([sQuery(id+"F7.wireOp",EDGE,"E67")])]})]});
            fillet(context, id + "F14", {"entities" : qUnion([Q0, Q1, Q2, Q3, Q4, Q5]), "radius" : 3 * mm, "tangentPropagation" : true, "allowEdgeOverflow" : false});
        }
        {
            var Q0;
            Q0=makeQuery(id+"F1.opExtrude","CAP_EDGE",EDGE,{"disambiguationData":[OSD([sQuery(id+"F0.wireOp",EDGE,"E1.bottom")])],"isStart":false});
            fillet(context, id + "F15", {"entities" : qUnion([Q0]), "radius" : 2 * mm, "tangentPropagation" : true, "allowEdgeOverflow" : false});
        }
        {
            var Q0;
            {var subQ0=sQuery(id+"F0.wireOp",EDGE,"E21.filletArc");var subQ1=sQuery(id+"F0.wireOp",EDGE,"E7");var subQ2=sQuery(id+"F0.wireOp",EDGE,"E6");var subQ3=sQuery(id+"F0.wireOp",EDGE,"E5");var subQ4=sQuery(id+"F0.wireOp",EDGE,"E4");var subQ5=sQuery(id+"F0.wireOp",EDGE,"E22.filletArc");var subQ6=sQuery(id+"F0.wireOp",EDGE,"E1.bottom");var subQ7=sQuery(id+"F0.wireOp",EDGE,"E1.right");var subQ8=sQuery(id+"F0.wireOp",EDGE,"E1.top");var subQ9=sQuery(id+"F0.wireOp",EDGE,"E1.left");var subQ10=sQuery(id+"F0.wireOp",EDGE,"E23.filletArc");var subQ11=sQuery(id+"F0.wireOp",EDGE,"E24.filletArc");Q0=makeQuery(id+"F2.boolean.opBoolean","SPLIT",FACE,{"disambiguationData":[TD([makeQuery(id+"F1.opExtrude","SWEPT_FACE",FACE,{"disambiguationData":[OSD([subQ6])]})])],"derivedFrom":makeQuery(id+"F1.opExtrude","CAP_FACE",FACE,{"disambiguationData":[OSD([subQ6,subQ8,subQ9,subQ7,subQ4,subQ3,subQ2,subQ1,subQ0,subQ5,subQ10,subQ11])],"isStart":true})});}
            var sketch = newSketch(context, id + "F16", { "sketchPlane" : qUnion([Q0])});
            skLineSegment(sketch, "E79", {"start": v(0, 90) * mm, "end": v(0, 120) * mm, "construction": true});
            skCircle(sketch, "E80", {"center": v(0, 120) * mm, "radius": 6 * mm});
            skArc(sketch, "E81", {"start": v(15, 120) * mm, "mid": v(0.23, 135) * mm, "end": v(-15, 120.46) * mm});
            skLineSegment(sketch, "E82", {"start": v(-14.88, 108) * mm, "end": v(-32.88, 90) * mm});
            skLineSegment(sketch, "E83", {"start": v(-14.88, 108) * mm, "end": v(-15, 120.46) * mm});
            skLineSegment(sketch, "E84", {"start": v(15, 120) * mm, "end": v(15, 108) * mm});
            skLineSegment(sketch, "E85", {"start": v(15, 108) * mm, "end": v(33, 90) * mm});
            skLineSegment(sketch, "E86", {"start": v(-80, 0) * mm, "end": v(80, 0) * mm, "construction": true});
            skLineSegment(sketch, "E87.MirrorCS", {"start": v(-14.88, -108) * mm, "end": v(-15, -120.46) * mm});
            skArc(sketch, "E88.MirrorCS", {"start": v(15, -120) * mm, "mid": v(0.23, -135) * mm, "end": v(-15, -120.46) * mm});
            skCircle(sketch, "E89.MirrorC", {"center": v(0, -120) * mm, "radius": 6 * mm});
            skLineSegment(sketch, "E90.MirrorCS", {"start": v(15, -120) * mm, "end": v(15, -108) * mm});
            skLineSegment(sketch, "E91.MirrorCS", {"start": v(15, -108) * mm, "end": v(33, -90) * mm});
            skLineSegment(sketch, "E92.MirrorCS", {"start": v(-14.88, -108) * mm, "end": v(-32.88, -90) * mm});
            skLineSegment(sketch, "E93.MirrorCS", {"start": v(0, -90) * mm, "end": v(0, -120) * mm, "construction": true});
            skSolve(sketch);
        }
        {
            var Q0;
            Q0=makeQuery(id+"F16.imprint","IMPRINT",FACE,{"disambiguationData":[TD([[makeQuery(id+"F16.imprint","IMPRINT",EDGE,{"derivedFrom":makeQuery(id+"F1.opExtrude","CAP_EDGE",EDGE,{"disambiguationData":[OSD([sQuery(id+"F0.wireOp",EDGE,"E1.left")])],"isStart":true})}),-1.0]])]});
            var Q1;
            Q1=makeQuery(id+"F16.imprint","IMPRINT",FACE,{"disambiguationData":[TD([[makeQuery(id+"F16.imprint","IMPRINT",EDGE,{"derivedFrom":sQuery(id+"F16.wireOp",EDGE,"E80")}),-1.0]])]});
            var Q2;
            Q2=makeQuery(id+"F16.imprint","IMPRINT",FACE,{"disambiguationData":[TD([[makeQuery(id+"F16.imprint","IMPRINT",EDGE,{"derivedFrom":sQuery(id+"F16.wireOp",EDGE,"E87.MirrorCS")}),1.0]])]});
            extrude(context, id + "F17", {"entities" : qUnion([Q0, Q1, Q2]), "operationType" : NewBodyOperationType.ADD, "depth" : 3 * mm});
        }
    });
